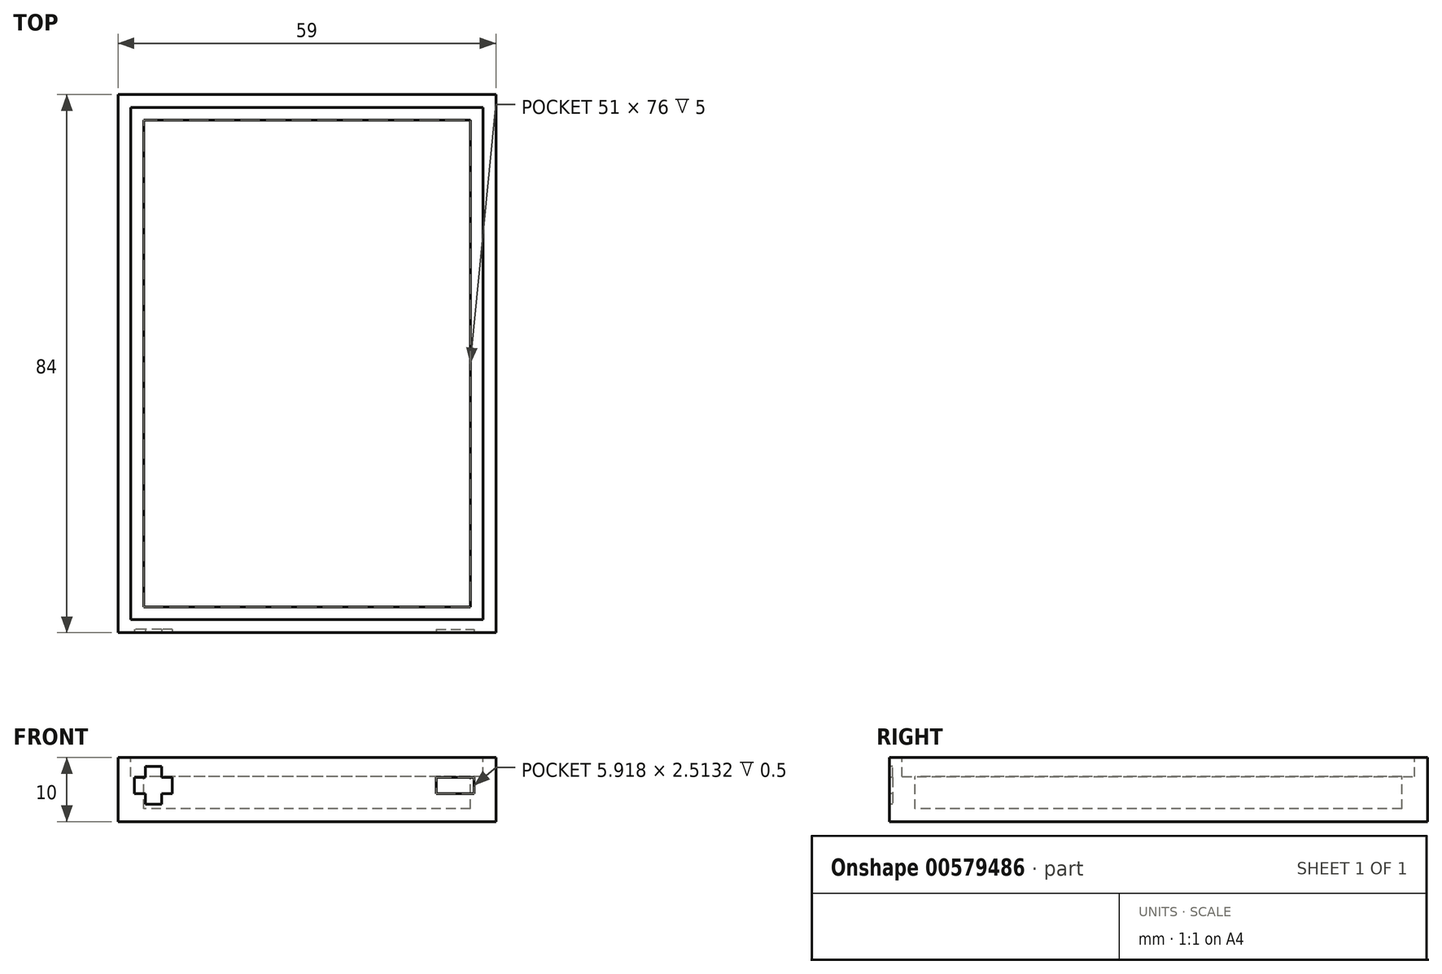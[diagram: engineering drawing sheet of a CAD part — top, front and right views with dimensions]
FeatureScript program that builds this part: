
annotation { "Feature Type Name" : "Feature", "Feature Type Description" : "" }
export const myFeature = defineFeature(function(context is Context, id is Id, definition is map)
    precondition{}
    {
        {
            var Q0;
            Q0=qCreatedBy(makeId("Top.planeOp"),FACE);
            var sketch = newSketch(context, id + "F0", { "sketchPlane" : qUnion([Q0])});
            skLineSegment(sketch, "E0.bottom", {"start": v(-28.61, 53.53) * mm, "end": v(30.39, 53.53) * mm});
            skLineSegment(sketch, "E0.top", {"start": v(-28.61, -30.47) * mm, "end": v(30.39, -30.47) * mm});
            skLineSegment(sketch, "E0.left", {"start": v(-28.61, 53.53) * mm, "end": v(-28.61, -30.47) * mm});
            skLineSegment(sketch, "E0.right", {"start": v(30.39, 53.53) * mm, "end": v(30.39, -30.47) * mm});
            skSolve(sketch);
        }
        {
            var Q0;
            Q0=makeQuery(id+"F0.imprint","IMPRINT",FACE,{"disambiguationData":[TD([[makeQuery(id+"F0.imprint","IMPRINT",EDGE,{"derivedFrom":sQuery(id+"F0.wireOp",EDGE,"E0.bottom")}),-1.0]])]});
            extrude(context, id + "F1", {"entities" : qUnion([Q0]), "depth" : 10 * mm, "offsetDistance" : 25 * mm});
        }
        {
            var Q0;
            Q0=makeQuery(id+"F1.opExtrude","CAP_FACE",FACE,{"disambiguationData":[OSD([sQuery(id+"F0.wireOp",EDGE,"E0.bottom"),sQuery(id+"F0.wireOp",EDGE,"E0.top"),sQuery(id+"F0.wireOp",EDGE,"E0.left"),sQuery(id+"F0.wireOp",EDGE,"E0.right")])],"isStart":false});
            var sketch = newSketch(context, id + "F2", { "sketchPlane" : qUnion([Q0])});
            skLineSegment(sketch, "E1.bottom", {"start": v(28.39, -28.47) * mm, "end": v(-26.61, -28.47) * mm});
            skLineSegment(sketch, "E1.top", {"start": v(28.39, 51.53) * mm, "end": v(-26.61, 51.53) * mm});
            skLineSegment(sketch, "E1.left", {"start": v(28.39, -28.47) * mm, "end": v(28.39, 51.53) * mm});
            skLineSegment(sketch, "E1.right", {"start": v(-26.61, -28.47) * mm, "end": v(-26.61, 51.53) * mm});
            skSolve(sketch);
        }
        {
            var Q0;
            Q0 = qSketchRegion(id + "F2", true);
            extrude(context, id + "F3", {"entities" : qUnion([Q0]), "operationType" : NewBodyOperationType.REMOVE, "oppositeDirection" : true, "depth" : 3 * mm, "offsetDistance" : 25 * mm});
        }
        {
            var Q0;
            Q0=makeQuery(id+"F3.boolean.opBoolean","COPY",FACE,{"derivedFrom":makeQuery(id+"F3.opExtrude","CAP_FACE",FACE,{"disambiguationData":[OSD([sQuery(id+"F2.wireOp",EDGE,"E1.bottom"),sQuery(id+"F2.wireOp",EDGE,"E1.top"),sQuery(id+"F2.wireOp",EDGE,"E1.left"),sQuery(id+"F2.wireOp",EDGE,"E1.right")])],"isStart":false})});
            var sketch = newSketch(context, id + "F4", { "sketchPlane" : qUnion([Q0])});
            skLineSegment(sketch, "E2.bottom", {"start": v(26.39, 49.53) * mm, "end": v(-24.61, 49.53) * mm});
            skLineSegment(sketch, "E2.top", {"start": v(26.39, -26.47) * mm, "end": v(-24.61, -26.47) * mm});
            skLineSegment(sketch, "E2.left", {"start": v(26.39, 49.53) * mm, "end": v(26.39, -26.47) * mm});
            skLineSegment(sketch, "E2.right", {"start": v(-24.61, 49.53) * mm, "end": v(-24.61, -26.47) * mm});
            skSolve(sketch);
        }
        {
            var Q0;
            Q0 = qSketchRegion(id + "F4", true);
            extrude(context, id + "F5", {"entities" : qUnion([Q0]), "operationType" : NewBodyOperationType.REMOVE, "oppositeDirection" : true, "depth" : 5 * mm, "offsetDistance" : 25 * mm});
        }
        {
            var Q0;
            Q0=makeQuery(id+"F1.opExtrude","SWEPT_FACE",FACE,{"disambiguationData":[OSD([sQuery(id+"F0.wireOp",EDGE,"E0.top")])]});
            var sketch = newSketch(context, id + "F6", { "sketchPlane" : qUnion([Q0])});
            skLineSegment(sketch, "E3", {"start": v(21.06, 4.38) * mm, "end": v(26.98, 4.38) * mm});
            skLineSegment(sketch, "E4", {"start": v(26.98, 4.38) * mm, "end": v(26.98, 6.9) * mm});
            skLineSegment(sketch, "E5", {"start": v(26.98, 6.9) * mm, "end": v(21.06, 6.9) * mm});
            skLineSegment(sketch, "E6", {"start": v(21.06, 6.9) * mm, "end": v(21.06, 4.38) * mm});
            skLineSegment(sketch, "E7", {"start": v(-20.12, 6.9) * mm, "end": v(-21.82, 6.9) * mm});
            skPoint(sketch, "E7.startSnap0", {"position": v(24.02, 6.9) * mm});
            skLineSegment(sketch, "E8", {"start": v(-21.82, 6.9) * mm, "end": v(-21.82, 8.6) * mm});
            skLineSegment(sketch, "E9", {"start": v(-21.82, 8.6) * mm, "end": v(-24.34, 8.6) * mm});
            skLineSegment(sketch, "E10", {"start": v(-24.34, 8.6) * mm, "end": v(-24.34, 6.9) * mm});
            skLineSegment(sketch, "E11", {"start": v(-24.34, 6.9) * mm, "end": v(-26.04, 6.9) * mm});
            skLineSegment(sketch, "E12", {"start": v(-26.04, 6.9) * mm, "end": v(-26.04, 4.38) * mm});
            skLineSegment(sketch, "E13", {"start": v(-26.04, 4.38) * mm, "end": v(-24.34, 4.38) * mm});
            skLineSegment(sketch, "E14", {"start": v(-24.34, 4.38) * mm, "end": v(-24.34, 2.68) * mm});
            skLineSegment(sketch, "E15", {"start": v(-24.34, 2.68) * mm, "end": v(-21.82, 2.68) * mm});
            skLineSegment(sketch, "E16", {"start": v(-21.82, 2.68) * mm, "end": v(-21.82, 4.38) * mm});
            skLineSegment(sketch, "E17", {"start": v(-21.82, 4.38) * mm, "end": v(-20.12, 4.38) * mm});
            skLineSegment(sketch, "E18", {"start": v(-20.12, 4.38) * mm, "end": v(-20.12, 6.9) * mm});
            skSolve(sketch);
        }
        {
            var Q0;
            Q0=makeQuery(id+"F6.imprint","IMPRINT",FACE,{"disambiguationData":[TD([[makeQuery(id+"F6.imprint","IMPRINT",EDGE,{"derivedFrom":sQuery(id+"F6.wireOp",EDGE,"E7")}),1.0]])]});
            var Q1;
            Q1=makeQuery(id+"F6.imprint","IMPRINT",FACE,{"disambiguationData":[TD([[makeQuery(id+"F6.imprint","IMPRINT",EDGE,{"derivedFrom":sQuery(id+"F6.wireOp",EDGE,"E3")}),1.0]])]});
            extrude(context, id + "F7", {"entities" : qUnion([Q0, Q1]), "operationType" : NewBodyOperationType.REMOVE, "oppositeDirection" : true, "depth" : .5 * mm, "offsetDistance" : 25 * mm});
        }
    });
